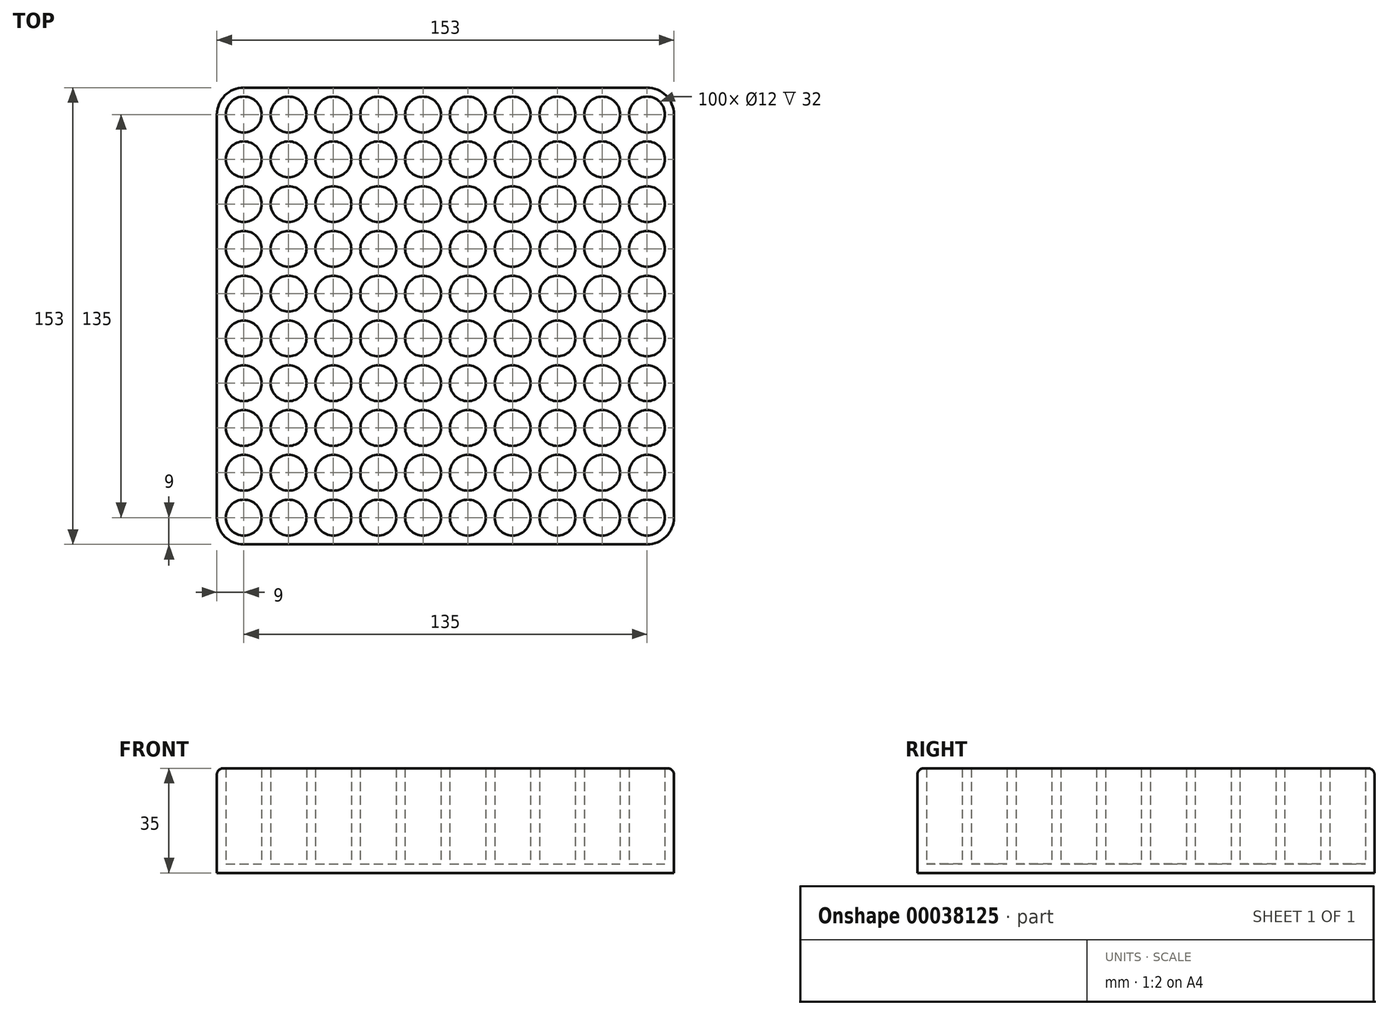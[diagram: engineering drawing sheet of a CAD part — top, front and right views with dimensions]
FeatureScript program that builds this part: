
annotation { "Feature Type Name" : "Feature", "Feature Type Description" : "" }
export const myFeature = defineFeature(function(context is Context, id is Id, definition is map)
    precondition{}
    {
        {
            var Q0;
            Q0=qCreatedBy(makeId("Top.planeOp"),FACE);
            var sketch = newSketch(context, id + "F0", { "sketchPlane" : qUnion([Q0])});
            skLineSegment(sketch, "E0.bottom", {"start": v(0, 0) * mm, "end": v(153, 0) * mm});
            skLineSegment(sketch, "E0.top", {"start": v(0, 153) * mm, "end": v(153, 153) * mm});
            skLineSegment(sketch, "E0.left", {"start": v(0, 0) * mm, "end": v(0, 153) * mm});
            skLineSegment(sketch, "E0.right", {"start": v(153, 0) * mm, "end": v(153, 153) * mm});
            skSolve(sketch);
        }
        {
            var Q0;
            Q0=makeQuery(id+"F0.imprint","IMPRINT",FACE,{"disambiguationData":[TD([[makeQuery(id+"F0.imprint","IMPRINT",EDGE,{"derivedFrom":sQuery(id+"F0.wireOp",EDGE,"E0.bottom")}),1.0]])]});
            extrude(context, id + "F1", {"entities" : qUnion([Q0]), "depth" : 35 * mm});
        }
        {
            var Q0;
            Q0=makeQuery(id+"F1.opExtrude","CAP_FACE",FACE,{"disambiguationData":[OSD([sQuery(id+"F0.wireOp",EDGE,"E0.bottom"),sQuery(id+"F0.wireOp",EDGE,"E0.top"),sQuery(id+"F0.wireOp",EDGE,"E0.left"),sQuery(id+"F0.wireOp",EDGE,"E0.right")])],"isStart":false});
            var sketch = newSketch(context, id + "F2", { "sketchPlane" : qUnion([Q0])});
            skCircle(sketch, "E1", {"center": v(9, 144) * mm, "radius": 6 * mm});
            skCircle(sketch, "E2.0.1.0", {"center": v(9, 129) * mm, "radius": 6 * mm});
            skCircle(sketch, "E2.0.2.0", {"center": v(9, 114) * mm, "radius": 6 * mm});
            skCircle(sketch, "E2.0.3.0", {"center": v(9, 99) * mm, "radius": 6 * mm});
            skCircle(sketch, "E2.0.4.0", {"center": v(9, 84) * mm, "radius": 6 * mm});
            skCircle(sketch, "E2.0.5.0", {"center": v(9, 69) * mm, "radius": 6 * mm});
            skCircle(sketch, "E2.0.6.0", {"center": v(9, 54) * mm, "radius": 6 * mm});
            skCircle(sketch, "E2.0.7.0", {"center": v(9, 39) * mm, "radius": 6 * mm});
            skCircle(sketch, "E2.0.8.0", {"center": v(9, 24) * mm, "radius": 6 * mm});
            skCircle(sketch, "E2.0.9.0", {"center": v(9, 9) * mm, "radius": 6 * mm});
            skCircle(sketch, "E2.1.0.0", {"center": v(24, 144) * mm, "radius": 6 * mm});
            skCircle(sketch, "E2.1.1.0", {"center": v(24, 129) * mm, "radius": 6 * mm});
            skCircle(sketch, "E2.1.2.0", {"center": v(24, 114) * mm, "radius": 6 * mm});
            skCircle(sketch, "E2.1.3.0", {"center": v(24, 99) * mm, "radius": 6 * mm});
            skCircle(sketch, "E2.1.4.0", {"center": v(24, 84) * mm, "radius": 6 * mm});
            skCircle(sketch, "E2.1.5.0", {"center": v(24, 69) * mm, "radius": 6 * mm});
            skCircle(sketch, "E2.1.6.0", {"center": v(24, 54) * mm, "radius": 6 * mm});
            skCircle(sketch, "E2.1.7.0", {"center": v(24, 39) * mm, "radius": 6 * mm});
            skCircle(sketch, "E2.1.8.0", {"center": v(24, 24) * mm, "radius": 6 * mm});
            skCircle(sketch, "E2.1.9.0", {"center": v(24, 9) * mm, "radius": 6 * mm});
            skCircle(sketch, "E2.2.0.0", {"center": v(39, 144) * mm, "radius": 6 * mm});
            skCircle(sketch, "E2.2.1.0", {"center": v(39, 129) * mm, "radius": 6 * mm});
            skCircle(sketch, "E2.2.2.0", {"center": v(39, 114) * mm, "radius": 6 * mm});
            skCircle(sketch, "E2.2.3.0", {"center": v(39, 99) * mm, "radius": 6 * mm});
            skCircle(sketch, "E2.2.4.0", {"center": v(39, 84) * mm, "radius": 6 * mm});
            skCircle(sketch, "E2.2.5.0", {"center": v(39, 69) * mm, "radius": 6 * mm});
            skCircle(sketch, "E2.2.6.0", {"center": v(39, 54) * mm, "radius": 6 * mm});
            skCircle(sketch, "E2.2.7.0", {"center": v(39, 39) * mm, "radius": 6 * mm});
            skCircle(sketch, "E2.2.8.0", {"center": v(39, 24) * mm, "radius": 6 * mm});
            skCircle(sketch, "E2.2.9.0", {"center": v(39, 9) * mm, "radius": 6 * mm});
            skCircle(sketch, "E2.3.0.0", {"center": v(54, 144) * mm, "radius": 6 * mm});
            skCircle(sketch, "E2.3.1.0", {"center": v(54, 129) * mm, "radius": 6 * mm});
            skCircle(sketch, "E2.3.2.0", {"center": v(54, 114) * mm, "radius": 6 * mm});
            skCircle(sketch, "E2.3.3.0", {"center": v(54, 99) * mm, "radius": 6 * mm});
            skCircle(sketch, "E2.3.4.0", {"center": v(54, 84) * mm, "radius": 6 * mm});
            skCircle(sketch, "E2.3.5.0", {"center": v(54, 69) * mm, "radius": 6 * mm});
            skCircle(sketch, "E2.3.6.0", {"center": v(54, 54) * mm, "radius": 6 * mm});
            skCircle(sketch, "E2.3.7.0", {"center": v(54, 39) * mm, "radius": 6 * mm});
            skCircle(sketch, "E2.3.8.0", {"center": v(54, 24) * mm, "radius": 6 * mm});
            skCircle(sketch, "E2.3.9.0", {"center": v(54, 9) * mm, "radius": 6 * mm});
            skCircle(sketch, "E2.4.0.0", {"center": v(69, 144) * mm, "radius": 6 * mm});
            skCircle(sketch, "E2.4.1.0", {"center": v(69, 129) * mm, "radius": 6 * mm});
            skCircle(sketch, "E2.4.2.0", {"center": v(69, 114) * mm, "radius": 6 * mm});
            skCircle(sketch, "E2.4.3.0", {"center": v(69, 99) * mm, "radius": 6 * mm});
            skCircle(sketch, "E2.4.4.0", {"center": v(69, 84) * mm, "radius": 6 * mm});
            skCircle(sketch, "E2.4.5.0", {"center": v(69, 69) * mm, "radius": 6 * mm});
            skCircle(sketch, "E2.4.6.0", {"center": v(69, 54) * mm, "radius": 6 * mm});
            skCircle(sketch, "E2.4.7.0", {"center": v(69, 39) * mm, "radius": 6 * mm});
            skCircle(sketch, "E2.4.8.0", {"center": v(69, 24) * mm, "radius": 6 * mm});
            skCircle(sketch, "E2.4.9.0", {"center": v(69, 9) * mm, "radius": 6 * mm});
            skCircle(sketch, "E2.5.0.0", {"center": v(84, 144) * mm, "radius": 6 * mm});
            skCircle(sketch, "E2.5.1.0", {"center": v(84, 129) * mm, "radius": 6 * mm});
            skCircle(sketch, "E2.5.2.0", {"center": v(84, 114) * mm, "radius": 6 * mm});
            skCircle(sketch, "E2.5.3.0", {"center": v(84, 99) * mm, "radius": 6 * mm});
            skCircle(sketch, "E2.5.4.0", {"center": v(84, 84) * mm, "radius": 6 * mm});
            skCircle(sketch, "E2.5.5.0", {"center": v(84, 69) * mm, "radius": 6 * mm});
            skCircle(sketch, "E2.5.6.0", {"center": v(84, 54) * mm, "radius": 6 * mm});
            skCircle(sketch, "E2.5.7.0", {"center": v(84, 39) * mm, "radius": 6 * mm});
            skCircle(sketch, "E2.5.8.0", {"center": v(84, 24) * mm, "radius": 6 * mm});
            skCircle(sketch, "E2.5.9.0", {"center": v(84, 9) * mm, "radius": 6 * mm});
            skCircle(sketch, "E2.6.0.0", {"center": v(99, 144) * mm, "radius": 6 * mm});
            skCircle(sketch, "E2.6.1.0", {"center": v(99, 129) * mm, "radius": 6 * mm});
            skCircle(sketch, "E2.6.2.0", {"center": v(99, 114) * mm, "radius": 6 * mm});
            skCircle(sketch, "E2.6.3.0", {"center": v(99, 99) * mm, "radius": 6 * mm});
            skCircle(sketch, "E2.6.4.0", {"center": v(99, 84) * mm, "radius": 6 * mm});
            skCircle(sketch, "E2.6.5.0", {"center": v(99, 69) * mm, "radius": 6 * mm});
            skCircle(sketch, "E2.6.6.0", {"center": v(99, 54) * mm, "radius": 6 * mm});
            skCircle(sketch, "E2.6.7.0", {"center": v(99, 39) * mm, "radius": 6 * mm});
            skCircle(sketch, "E2.6.8.0", {"center": v(99, 24) * mm, "radius": 6 * mm});
            skCircle(sketch, "E2.6.9.0", {"center": v(99, 9) * mm, "radius": 6 * mm});
            skCircle(sketch, "E2.7.0.0", {"center": v(114, 144) * mm, "radius": 6 * mm});
            skCircle(sketch, "E2.7.1.0", {"center": v(114, 129) * mm, "radius": 6 * mm});
            skCircle(sketch, "E2.7.2.0", {"center": v(114, 114) * mm, "radius": 6 * mm});
            skCircle(sketch, "E2.7.3.0", {"center": v(114, 99) * mm, "radius": 6 * mm});
            skCircle(sketch, "E2.7.4.0", {"center": v(114, 84) * mm, "radius": 6 * mm});
            skCircle(sketch, "E2.7.5.0", {"center": v(114, 69) * mm, "radius": 6 * mm});
            skCircle(sketch, "E2.7.6.0", {"center": v(114, 54) * mm, "radius": 6 * mm});
            skCircle(sketch, "E2.7.7.0", {"center": v(114, 39) * mm, "radius": 6 * mm});
            skCircle(sketch, "E2.7.8.0", {"center": v(114, 24) * mm, "radius": 6 * mm});
            skCircle(sketch, "E2.7.9.0", {"center": v(114, 9) * mm, "radius": 6 * mm});
            skCircle(sketch, "E2.8.0.0", {"center": v(129, 144) * mm, "radius": 6 * mm});
            skCircle(sketch, "E2.8.1.0", {"center": v(129, 129) * mm, "radius": 6 * mm});
            skCircle(sketch, "E2.8.2.0", {"center": v(129, 114) * mm, "radius": 6 * mm});
            skCircle(sketch, "E2.8.3.0", {"center": v(129, 99) * mm, "radius": 6 * mm});
            skCircle(sketch, "E2.8.4.0", {"center": v(129, 84) * mm, "radius": 6 * mm});
            skCircle(sketch, "E2.8.5.0", {"center": v(129, 69) * mm, "radius": 6 * mm});
            skCircle(sketch, "E2.8.6.0", {"center": v(129, 54) * mm, "radius": 6 * mm});
            skCircle(sketch, "E2.8.7.0", {"center": v(129, 39) * mm, "radius": 6 * mm});
            skCircle(sketch, "E2.8.8.0", {"center": v(129, 24) * mm, "radius": 6 * mm});
            skCircle(sketch, "E2.8.9.0", {"center": v(129, 9) * mm, "radius": 6 * mm});
            skCircle(sketch, "E2.9.0.0", {"center": v(144, 144) * mm, "radius": 6 * mm});
            skCircle(sketch, "E2.9.1.0", {"center": v(144, 129) * mm, "radius": 6 * mm});
            skCircle(sketch, "E2.9.2.0", {"center": v(144, 114) * mm, "radius": 6 * mm});
            skCircle(sketch, "E2.9.3.0", {"center": v(144, 99) * mm, "radius": 6 * mm});
            skCircle(sketch, "E2.9.4.0", {"center": v(144, 84) * mm, "radius": 6 * mm});
            skCircle(sketch, "E2.9.5.0", {"center": v(144, 69) * mm, "radius": 6 * mm});
            skCircle(sketch, "E2.9.6.0", {"center": v(144, 54) * mm, "radius": 6 * mm});
            skCircle(sketch, "E2.9.7.0", {"center": v(144, 39) * mm, "radius": 6 * mm});
            skCircle(sketch, "E2.9.8.0", {"center": v(144, 24) * mm, "radius": 6 * mm});
            skCircle(sketch, "E2.9.9.0", {"center": v(144, 9) * mm, "radius": 6 * mm});
            skLineSegment(sketch, "E2.direction1", {"start": v(9, 144) * mm, "end": v(24, 144) * mm, "construction": true});
            skLineSegment(sketch, "E2.direction2", {"start": v(9, 144) * mm, "end": v(9, 129) * mm, "construction": true});
            skSolve(sketch);
        }
        {
            var Q0;
            Q0=sQuery(id+"F2.wireOp",VERTEX,"E1.center");
            var Q1;
            Q1=sQuery(id+"F2.wireOp",VERTEX,"E2.0.1.0.center");
            var Q2;
            Q2=sQuery(id+"F2.wireOp",VERTEX,"E2.0.2.0.center");
            var Q3;
            Q3=sQuery(id+"F2.wireOp",VERTEX,"E2.0.3.0.center");
            var Q4;
            Q4=sQuery(id+"F2.wireOp",VERTEX,"E2.0.4.0.center");
            var Q5;
            Q5=sQuery(id+"F2.wireOp",VERTEX,"E2.0.5.0.center");
            var Q6;
            Q6=sQuery(id+"F2.wireOp",VERTEX,"E2.0.6.0.center");
            var Q7;
            Q7=sQuery(id+"F2.wireOp",VERTEX,"E2.0.7.0.center");
            var Q8;
            Q8=sQuery(id+"F2.wireOp",VERTEX,"E2.0.8.0.center");
            var Q9;
            Q9=sQuery(id+"F2.wireOp",VERTEX,"E2.0.9.0.center");
            var Q10;
            Q10=sQuery(id+"F2.wireOp",VERTEX,"E2.1.9.0.center");
            var Q11;
            Q11=sQuery(id+"F2.wireOp",VERTEX,"E2.1.8.0.center");
            var Q12;
            Q12=sQuery(id+"F2.wireOp",VERTEX,"E2.1.7.0.center");
            var Q13;
            Q13=sQuery(id+"F2.wireOp",VERTEX,"E2.1.6.0.center");
            var Q14;
            Q14=sQuery(id+"F2.wireOp",VERTEX,"E2.1.5.0.center");
            var Q15;
            Q15=sQuery(id+"F2.wireOp",VERTEX,"E2.1.4.0.center");
            var Q16;
            Q16=sQuery(id+"F2.wireOp",VERTEX,"E2.1.3.0.center");
            var Q17;
            Q17=sQuery(id+"F2.wireOp",VERTEX,"E2.1.2.0.center");
            var Q18;
            Q18=sQuery(id+"F2.wireOp",VERTEX,"E2.1.1.0.center");
            var Q19;
            Q19=sQuery(id+"F2.wireOp",VERTEX,"E2.direction1.end");
            var Q20;
            Q20=sQuery(id+"F2.wireOp",VERTEX,"E2.2.0.0.center");
            var Q21;
            Q21=sQuery(id+"F2.wireOp",VERTEX,"E2.3.0.0.center");
            var Q22;
            Q22=sQuery(id+"F2.wireOp",VERTEX,"E2.4.0.0.center");
            var Q23;
            Q23=sQuery(id+"F2.wireOp",VERTEX,"E2.5.0.0.center");
            var Q24;
            Q24=sQuery(id+"F2.wireOp",VERTEX,"E2.6.0.0.center");
            var Q25;
            Q25=sQuery(id+"F2.wireOp",VERTEX,"E2.7.0.0.center");
            var Q26;
            Q26=sQuery(id+"F2.wireOp",VERTEX,"E2.8.0.0.center");
            var Q27;
            Q27=sQuery(id+"F2.wireOp",VERTEX,"E2.9.0.0.center");
            var Q28;
            Q28=sQuery(id+"F2.wireOp",VERTEX,"E2.9.1.0.center");
            var Q29;
            Q29=sQuery(id+"F2.wireOp",VERTEX,"E2.8.1.0.center");
            var Q30;
            Q30=sQuery(id+"F2.wireOp",VERTEX,"E2.7.1.0.center");
            var Q31;
            Q31=sQuery(id+"F2.wireOp",VERTEX,"E2.6.1.0.center");
            var Q32;
            Q32=sQuery(id+"F2.wireOp",VERTEX,"E2.5.1.0.center");
            var Q33;
            Q33=sQuery(id+"F2.wireOp",VERTEX,"E2.4.1.0.center");
            var Q34;
            Q34=sQuery(id+"F2.wireOp",VERTEX,"E2.3.1.0.center");
            var Q35;
            Q35=sQuery(id+"F2.wireOp",VERTEX,"E2.2.1.0.center");
            var Q36;
            Q36=sQuery(id+"F2.wireOp",VERTEX,"E2.2.2.0.center");
            var Q37;
            Q37=sQuery(id+"F2.wireOp",VERTEX,"E2.2.3.0.center");
            var Q38;
            Q38=sQuery(id+"F2.wireOp",VERTEX,"E2.2.4.0.center");
            var Q39;
            Q39=sQuery(id+"F2.wireOp",VERTEX,"E2.2.5.0.center");
            var Q40;
            Q40=sQuery(id+"F2.wireOp",VERTEX,"E2.2.6.0.center");
            var Q41;
            Q41=sQuery(id+"F2.wireOp",VERTEX,"E2.2.7.0.center");
            var Q42;
            Q42=sQuery(id+"F2.wireOp",VERTEX,"E2.2.8.0.center");
            var Q43;
            Q43=sQuery(id+"F2.wireOp",VERTEX,"E2.2.9.0.center");
            var Q44;
            Q44=sQuery(id+"F2.wireOp",VERTEX,"E2.3.9.0.center");
            var Q45;
            Q45=sQuery(id+"F2.wireOp",VERTEX,"E2.3.8.0.center");
            var Q46;
            Q46=sQuery(id+"F2.wireOp",VERTEX,"E2.3.7.0.center");
            var Q47;
            Q47=sQuery(id+"F2.wireOp",VERTEX,"E2.3.6.0.center");
            var Q48;
            Q48=sQuery(id+"F2.wireOp",VERTEX,"E2.3.5.0.center");
            var Q49;
            Q49=sQuery(id+"F2.wireOp",VERTEX,"E2.3.4.0.center");
            var Q50;
            Q50=sQuery(id+"F2.wireOp",VERTEX,"E2.3.3.0.center");
            var Q51;
            Q51=sQuery(id+"F2.wireOp",VERTEX,"E2.3.2.0.center");
            var Q52;
            Q52=sQuery(id+"F2.wireOp",VERTEX,"E2.4.2.0.center");
            var Q53;
            Q53=sQuery(id+"F2.wireOp",VERTEX,"E2.4.3.0.center");
            var Q54;
            Q54=sQuery(id+"F2.wireOp",VERTEX,"E2.4.4.0.center");
            var Q55;
            Q55=sQuery(id+"F2.wireOp",VERTEX,"E2.4.5.0.center");
            var Q56;
            Q56=sQuery(id+"F2.wireOp",VERTEX,"E2.4.6.0.center");
            var Q57;
            Q57=sQuery(id+"F2.wireOp",VERTEX,"E2.4.7.0.center");
            var Q58;
            Q58=sQuery(id+"F2.wireOp",VERTEX,"E2.4.8.0.center");
            var Q59;
            Q59=sQuery(id+"F2.wireOp",VERTEX,"E2.4.9.0.center");
            var Q60;
            Q60=sQuery(id+"F2.wireOp",VERTEX,"E2.5.9.0.center");
            var Q61;
            Q61=sQuery(id+"F2.wireOp",VERTEX,"E2.5.8.0.center");
            var Q62;
            Q62=sQuery(id+"F2.wireOp",VERTEX,"E2.5.7.0.center");
            var Q63;
            Q63=sQuery(id+"F2.wireOp",VERTEX,"E2.5.6.0.center");
            var Q64;
            Q64=sQuery(id+"F2.wireOp",VERTEX,"E2.5.5.0.center");
            var Q65;
            Q65=sQuery(id+"F2.wireOp",VERTEX,"E2.5.4.0.center");
            var Q66;
            Q66=sQuery(id+"F2.wireOp",VERTEX,"E2.5.3.0.center");
            var Q67;
            Q67=sQuery(id+"F2.wireOp",VERTEX,"E2.5.2.0.center");
            var Q68;
            Q68=sQuery(id+"F2.wireOp",VERTEX,"E2.6.2.0.center");
            var Q69;
            Q69=sQuery(id+"F2.wireOp",VERTEX,"E2.6.3.0.center");
            var Q70;
            Q70=sQuery(id+"F2.wireOp",VERTEX,"E2.6.4.0.center");
            var Q71;
            Q71=sQuery(id+"F2.wireOp",VERTEX,"E2.6.5.0.center");
            var Q72;
            Q72=sQuery(id+"F2.wireOp",VERTEX,"E2.6.6.0.center");
            var Q73;
            Q73=sQuery(id+"F2.wireOp",VERTEX,"E2.6.7.0.center");
            var Q74;
            Q74=sQuery(id+"F2.wireOp",VERTEX,"E2.6.8.0.center");
            var Q75;
            Q75=sQuery(id+"F2.wireOp",VERTEX,"E2.6.9.0.center");
            var Q76;
            Q76=sQuery(id+"F2.wireOp",VERTEX,"E2.7.9.0.center");
            var Q77;
            Q77=sQuery(id+"F2.wireOp",VERTEX,"E2.8.9.0.center");
            var Q78;
            Q78=sQuery(id+"F2.wireOp",VERTEX,"E2.9.9.0.center");
            var Q79;
            Q79=sQuery(id+"F2.wireOp",VERTEX,"E2.9.8.0.center");
            var Q80;
            Q80=sQuery(id+"F2.wireOp",VERTEX,"E2.8.8.0.center");
            var Q81;
            Q81=sQuery(id+"F2.wireOp",VERTEX,"E2.7.8.0.center");
            var Q82;
            Q82=sQuery(id+"F2.wireOp",VERTEX,"E2.7.7.0.center");
            var Q83;
            Q83=sQuery(id+"F2.wireOp",VERTEX,"E2.8.7.0.center");
            var Q84;
            Q84=sQuery(id+"F2.wireOp",VERTEX,"E2.9.7.0.center");
            var Q85;
            Q85=sQuery(id+"F2.wireOp",VERTEX,"E2.9.6.0.center");
            var Q86;
            Q86=sQuery(id+"F2.wireOp",VERTEX,"E2.8.6.0.center");
            var Q87;
            Q87=sQuery(id+"F2.wireOp",VERTEX,"E2.7.6.0.center");
            var Q88;
            Q88=sQuery(id+"F2.wireOp",VERTEX,"E2.7.5.0.center");
            var Q89;
            Q89=sQuery(id+"F2.wireOp",VERTEX,"E2.8.5.0.center");
            var Q90;
            Q90=sQuery(id+"F2.wireOp",VERTEX,"E2.9.5.0.center");
            var Q91;
            Q91=sQuery(id+"F2.wireOp",VERTEX,"E2.9.4.0.center");
            var Q92;
            Q92=sQuery(id+"F2.wireOp",VERTEX,"E2.8.4.0.center");
            var Q93;
            Q93=sQuery(id+"F2.wireOp",VERTEX,"E2.7.4.0.center");
            var Q94;
            Q94=sQuery(id+"F2.wireOp",VERTEX,"E2.7.3.0.center");
            var Q95;
            Q95=sQuery(id+"F2.wireOp",VERTEX,"E2.7.2.0.center");
            var Q96;
            Q96=sQuery(id+"F2.wireOp",VERTEX,"E2.8.2.0.center");
            var Q97;
            Q97=sQuery(id+"F2.wireOp",VERTEX,"E2.8.3.0.center");
            var Q98;
            Q98=sQuery(id+"F2.wireOp",VERTEX,"E2.9.3.0.center");
            var Q99;
            Q99=sQuery(id+"F2.wireOp",VERTEX,"E2.9.2.0.center");
            var Q100;
            Q100=makeQuery(id+"F1.opExtrude","SWEPT_BODY",BODY,{"disambiguationData":[OSD([sQuery(id+"F0.wireOp",EDGE,"E0.bottom"),sQuery(id+"F0.wireOp",EDGE,"E0.top"),sQuery(id+"F0.wireOp",EDGE,"E0.left"),sQuery(id+"F0.wireOp",EDGE,"E0.right")])]});
            hole(context, id + "F3", {"style" : HoleStyle.SIMPLE, "holeDiameter" : 12 * mm, "endStyle" : HoleEndStyle.THROUGH, "locations" : qUnion([Q0, Q1, Q2, Q3, Q4, Q5, Q6, Q7, Q8, Q9, Q10, Q11, Q12, Q13, Q14, Q15, Q16, Q17, Q18, Q19, Q20, Q21, Q22, Q23, Q24, Q25, Q26, Q27, Q28, Q29, Q30, Q31, Q32, Q33, Q34, Q35, Q36, Q37, Q38, Q39, Q40, Q41, Q42, Q43, Q44, Q45, Q46, Q47, Q48, Q49, Q50, Q51, Q52, Q53, Q54, Q55, Q56, Q57, Q58, Q59, Q60, Q61, Q62, Q63, Q64, Q65, Q66, Q67, Q68, Q69, Q70, Q71, Q72, Q73, Q74, Q75, Q76, Q77, Q78, Q79, Q80, Q81, Q82, Q83, Q84, Q85, Q86, Q87, Q88, Q89, Q90, Q91, Q92, Q93, Q94, Q95, Q96, Q97, Q98, Q99]), "scope" : qUnion([Q100])});
        }
        {
            var Q0;
            Q0=makeQuery(id+"F1.opExtrude","SWEPT_EDGE",EDGE,{"disambiguationData":[OSD([sQuery(id+"F0.wireOp",EDGE,"E0.top"),sQuery(id+"F0.wireOp",EDGE,"E0.left")])]});
            var Q1;
            Q1=makeQuery(id+"F1.opExtrude","SWEPT_EDGE",EDGE,{"disambiguationData":[OSD([sQuery(id+"F0.wireOp",EDGE,"E0.bottom"),sQuery(id+"F0.wireOp",EDGE,"E0.left")])]});
            var Q2;
            Q2=makeQuery(id+"F1.opExtrude","SWEPT_EDGE",EDGE,{"disambiguationData":[OSD([sQuery(id+"F0.wireOp",EDGE,"E0.bottom"),sQuery(id+"F0.wireOp",EDGE,"E0.right")])]});
            var Q3;
            Q3=makeQuery(id+"F1.opExtrude","SWEPT_EDGE",EDGE,{"disambiguationData":[OSD([sQuery(id+"F0.wireOp",EDGE,"E0.top"),sQuery(id+"F0.wireOp",EDGE,"E0.right")])]});
            fillet(context, id + "F4", {"entities" : qUnion([Q0, Q1, Q2, Q3]), "radius" : 9 * mm, "tangentPropagation" : true, "allowEdgeOverflow" : false});
        }
        {
            var Q0;
            Q0=makeQuery(id+"F1.opExtrude","CAP_EDGE",EDGE,{"disambiguationData":[OSD([sQuery(id+"F0.wireOp",EDGE,"E0.bottom")])],"isStart":false});
            var Q1;
            {var subQ0=sQuery(id+"F0.wireOp",EDGE,"E0.bottom");var subQ1=sQuery(id+"F0.wireOp",EDGE,"E0.right");Q1=makeQuery(id+"F4.opFillet","BLEND_EDGE",EDGE,{"blendedFrom":[makeQuery(id+"F1.opExtrude","SWEPT_EDGE",EDGE,{"disambiguationData":[OSD([subQ0,subQ1])]}),makeQuery(id+"F1.opExtrude","CAP_FACE",FACE,{"disambiguationData":[OSD([subQ0,sQuery(id+"F0.wireOp",EDGE,"E0.top"),sQuery(id+"F0.wireOp",EDGE,"E0.left"),subQ1])],"isStart":false})],"blendedInto":[makeQuery(id+"F1.opExtrude","CAP_FACE",FACE,{"disambiguationData":[OSD([subQ0,sQuery(id+"F0.wireOp",EDGE,"E0.top"),sQuery(id+"F0.wireOp",EDGE,"E0.left"),subQ1])],"isStart":false})]});}
            var Q2;
            Q2=makeQuery(id+"F1.opExtrude","CAP_EDGE",EDGE,{"disambiguationData":[OSD([sQuery(id+"F0.wireOp",EDGE,"E0.right")])],"isStart":false});
            fillet(context, id + "F5", {"entities" : qUnion([Q0, Q1, Q2]), "radius" : 2 * mm, "tangentPropagation" : true, "allowEdgeOverflow" : false});
        }
        {
            var Q0;
            Q0=makeQuery(id+"F1.opExtrude","CAP_FACE",FACE,{"disambiguationData":[OSD([sQuery(id+"F0.wireOp",EDGE,"E0.bottom"),sQuery(id+"F0.wireOp",EDGE,"E0.top"),sQuery(id+"F0.wireOp",EDGE,"E0.left"),sQuery(id+"F0.wireOp",EDGE,"E0.right")])],"isStart":true});
            var sketch = newSketch(context, id + "F6", { "sketchPlane" : qUnion([Q0])});
            skLineSegment(sketch, "E3.0", {"start": v(9, 0) * mm, "end": v(144, 0) * mm});
            skArc(sketch, "E3.1", {"start": v(153, -9) * mm, "mid": v(150.36, -2.64) * mm, "end": v(144, 0) * mm});
            skLineSegment(sketch, "E3.2", {"start": v(153, -9) * mm, "end": v(153, -144) * mm});
            skArc(sketch, "E3.3", {"start": v(144, -153) * mm, "mid": v(150.36, -150.36) * mm, "end": v(153, -144) * mm});
            skLineSegment(sketch, "E3.4", {"start": v(9, -153) * mm, "end": v(144, -153) * mm});
            skArc(sketch, "E3.5", {"start": v(0, -144) * mm, "mid": v(2.64, -150.36) * mm, "end": v(9, -153) * mm});
            skLineSegment(sketch, "E3.6", {"start": v(0, -9) * mm, "end": v(0, -144) * mm});
            skArc(sketch, "E3.7", {"start": v(9, 0) * mm, "mid": v(2.64, -2.64) * mm, "end": v(0, -9) * mm});
            skSolve(sketch);
        }
        {
            var Q0;
            Q0 = qSketchRegion(id + "F6", true);
            extrude(context, id + "F7", {"entities" : qUnion([Q0]), "operationType" : NewBodyOperationType.ADD, "oppositeDirection" : true, "depth" : 3 * mm});
        }
    });
